# Revit family: Door-Slider-Fleetwood-3000-OX
name_source: partatom
category: Doors
revit_build: Autodesk Revit Architecture 2013 (Build: 20120221_2030(x64)
units: mm (PartAtom-declared; Revit-internal decimal feet)

## types (6) — shared parameters
1.25"_Sill = No
1.875"_Sill = Yes
3"_Sill = No
Analytic Construction = <None>
Arrow Location = 18 "
Centerline_1_Calc = 48 "
Configuration = OX
Equal_Centerlines = Yes
Exterior Wrap Overhang = 0.5 "
Frame_&_Panel = Aluminum, Anodized Clear
Function = Exterior
Glazing = Glass
Hardware = Stainless Steel, Brushed
Height = 96 "
Interior Wrap Overhang = 0.5 "
Manufacturer = Fleetwood Windows and Doors
Model = 3000
Panel_1 = 48.2791 "
Panel_2 = 48 "
Panel_Height_Fixed = 94.4215 "
Panel_Height_Sliding = 93.9845 "
Rough Height = 96.25 "
Rough Width = 96.5 "
Screen_2 = 48.196 "
Screen_Handle_Centerline = 40 "
Screen_Height = 94.875 "
Screen_Mesh = ULTRA_VUE
Screens = Yes
Sill_Height = 1.875 "
Thickness = 4.5 "
URL = www.fleetwoodusa.com
Wall Closure = By host
Width = 96 "
zero-valued in all types: Centerline_1

## per-type parameters (varying)
| type | Actuator_Height | Panel_1_Config | Panel_2_Config |
| Archetype Hardware_Archetype Narrow Fixed Stile | 53.75 " | 3000_Panel : Fixed Panel Archetype Narrow Stile | 3000_Panel : Active Lead Panel Right Archetype |
| Archetype Hardware_Archetype Fixed Stile | 53.75 " | 3000_Panel : Fixed Panel Archetype Stile | 3000_Panel : Active Lead Panel Right Archetype |
| Archetype Narrow Hardware_Narrow Fixed Stile | 46 " | 3000_Panel : Fixed Panel Narrow Fixed Stile | 3000_Panel : Active Lead Panel Right Archetype Narrow |
| Archetype Narrow Hardware_Archetype Narrow Fixed Stile | 46 " | 3000_Panel : Fixed Panel Archetype Narrow Stile | 3000_Panel : Active Lead Panel Right Archetype Narrow |
| Archetype Narrow Hardware_Archetype Fixed Stile | 46 " | 3000_Panel : Fixed Panel Archetype Stile | 3000_Panel : Active Lead Panel Right Archetype Narrow |
| Archetype Hardware_Narrow Fixed Stile | 53.75 " | 3000_Panel : Fixed Panel Narrow Fixed Stile | 3000_Panel : Active Lead Panel Right Archetype |

## geometry (parser evidence)
native form markers: Blend x34, Sweep x37
no freeform markers — native parametric forms only
